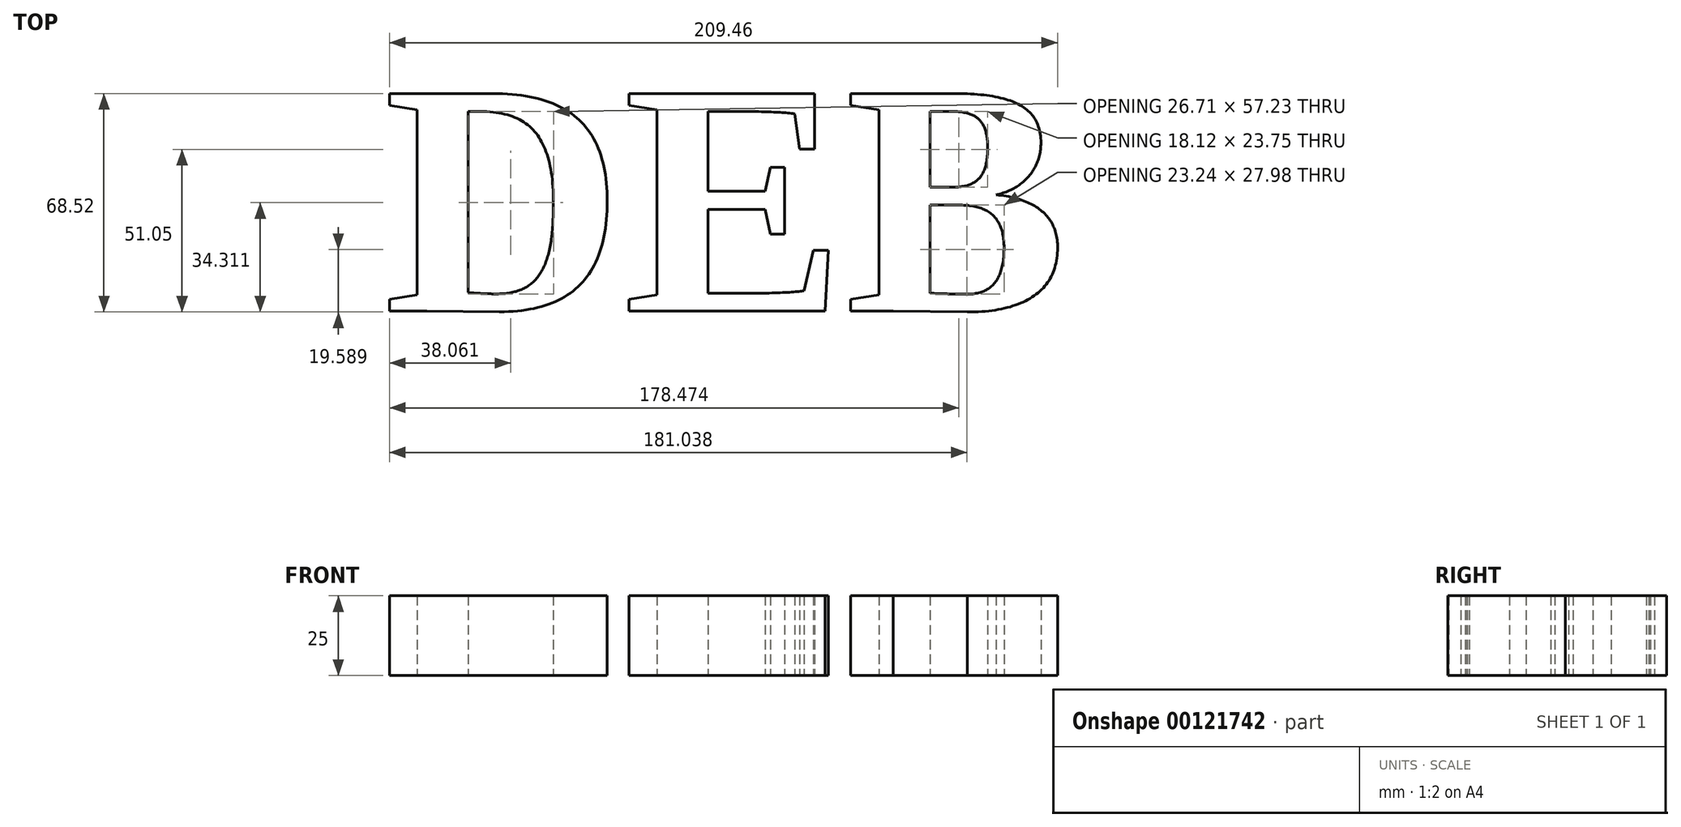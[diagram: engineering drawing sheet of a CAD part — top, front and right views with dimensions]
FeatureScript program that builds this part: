
annotation { "Feature Type Name" : "Feature", "Feature Type Description" : "" }
export const myFeature = defineFeature(function(context is Context, id is Id, definition is map)
    precondition{}
    {
        {
            var Q0;
            Q0=qCreatedBy(makeId("Top.planeOp"),FACE);
            var sketch = newSketch(context, id + "F0", { "sketchPlane" : qUnion([Q0])});
            skText(sketch, "E0", { "text": "DEB", "fontName": "Tinos-Bold.ttf"});
            const initialGuessF0  = {"E0": [-0.1677, 0, 1, 0, 0.075]};
            skSetInitialGuess(sketch, initialGuessF0);
            skSolve(sketch);
        }
        {
            var Q0;
            Q0 = qSketchRegion(id + "F0", true);
            extrude(context, id + "F1", {"entities" : qUnion([Q0]), "depth" : 25 * mm});
        }
    });
